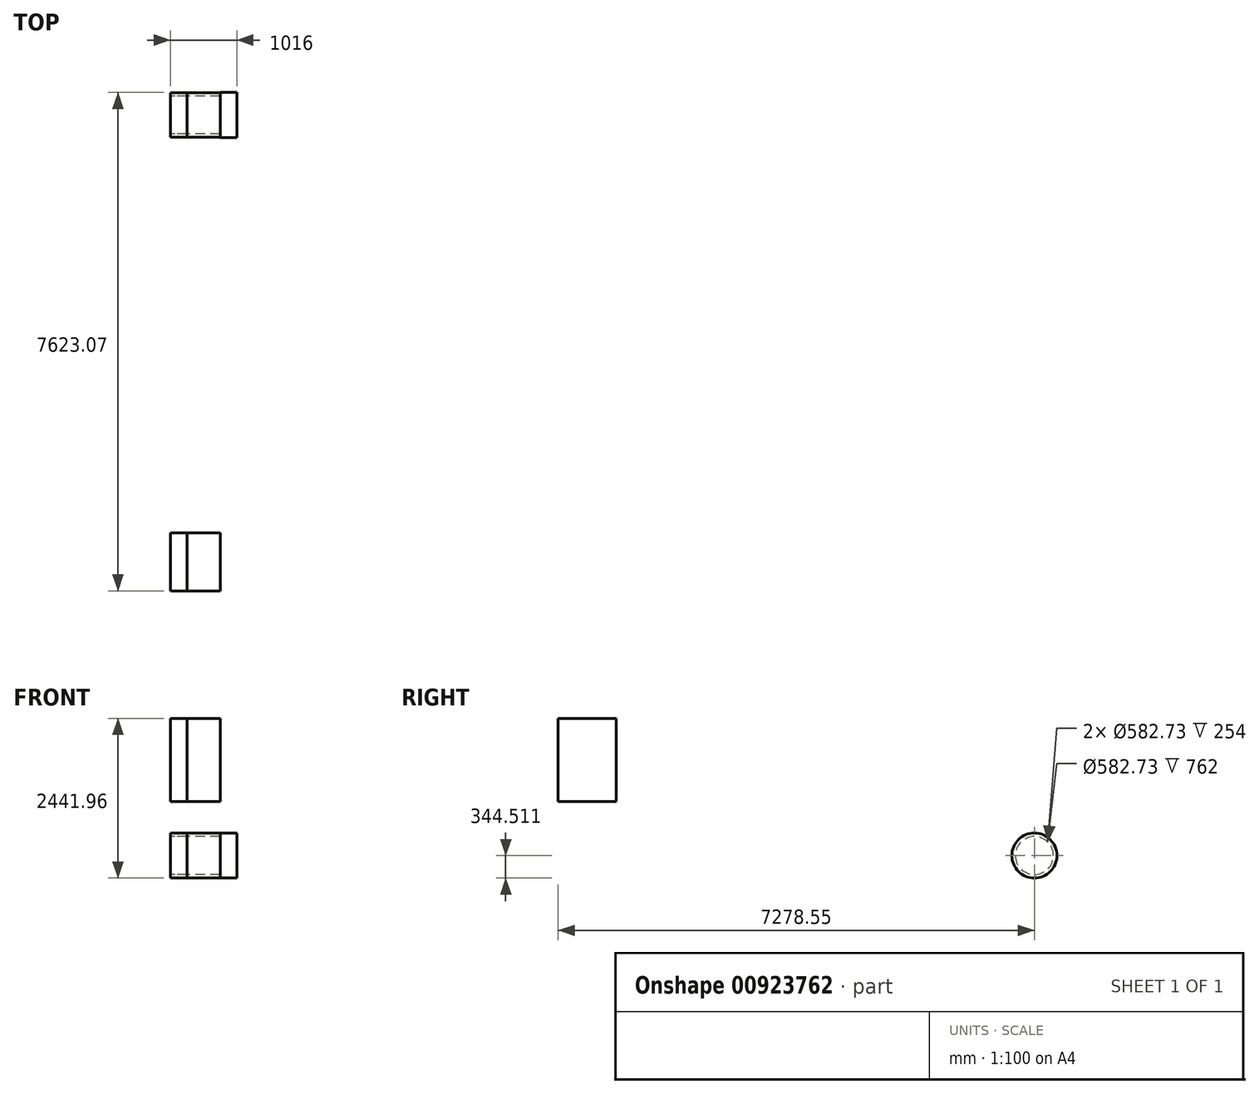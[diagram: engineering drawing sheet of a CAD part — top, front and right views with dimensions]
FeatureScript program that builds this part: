
annotation { "Feature Type Name" : "Feature", "Feature Type Description" : "" }
export const myFeature = defineFeature(function(context is Context, id is Id, definition is map)
    precondition{}
    {
        {
            var Q0;
            Q0=qCreatedBy(makeId("Right.planeOp"),FACE);
            var sketch = newSketch(context, id + "F0", { "sketchPlane" : qUnion([Q0])});
            skLineSegment(sketch, "E0.bottom", {"start": v(-8245.64, 2552.86) * mm, "end": v(-7356.64, 2552.86) * mm});
            skLineSegment(sketch, "E0.top", {"start": v(-8245.64, 1282.86) * mm, "end": v(-7356.64, 1282.86) * mm});
            skLineSegment(sketch, "E0.left", {"start": v(-8245.64, 2552.86) * mm, "end": v(-8245.64, 1282.86) * mm});
            skLineSegment(sketch, "E0.right", {"start": v(-7356.64, 2552.86) * mm, "end": v(-7356.64, 1282.86) * mm});
            skCircle(sketch, "E1", {"center": v(-967.09, 455.41) * mm, "radius": 341.94 * mm});
            skCircle(sketch, "E2", {"center": v(-967.09, 455.41) * mm, "radius": 291.36 * mm});
            skSolve(sketch);
        }
        {
            var Q0;
            Q0 = qSketchRegion(id + "F0", true);
            extrude(context, id + "F1", {"entities" : qUnion([Q0]), "depth" : 254 * mm, "offsetDistance" : 25.4 * mm});
        }
        {
            var Q0;
            Q0 = qSketchRegion(id + "F0", true);
            extrude(context, id + "F2", {"entities" : qUnion([Q0]), "depth" : 254 * mm, "offsetDistance" : 25.4 * mm});
        }
        {
            var Q0;
            Q0 = qSketchRegion(id + "F0", true);
            extrude(context, id + "F3", {"entities" : qUnion([Q0]), "depth" : 762 * mm, "offsetDistance" : 25.4 * mm});
        }
        {
            var Q0;
            Q0=makeQuery(id+"F3.opExtrude","CAP_FACE",FACE,{"disambiguationData":[OSD([sQuery(id+"F0.wireOp",EDGE,"E1"),sQuery(id+"F0.wireOp",EDGE,"E2")])],"isStart":false});
            var sketch = newSketch(context, id + "F4", { "sketchPlane" : qUnion([Q0])});
            skCircle(sketch, "E3", {"center": v(-967.09, 455.41) * mm, "radius": 344.52 * mm});
            skSolve(sketch);
        }
        {
            var Q0;
            Q0 = qSketchRegion(id + "F4", true);
            extrude(context, id + "F5", {"entities" : qUnion([Q0]), "operationType" : NewBodyOperationType.ADD, "depth" : 254 * mm, "offsetDistance" : 25.4 * mm});
        }
    });
